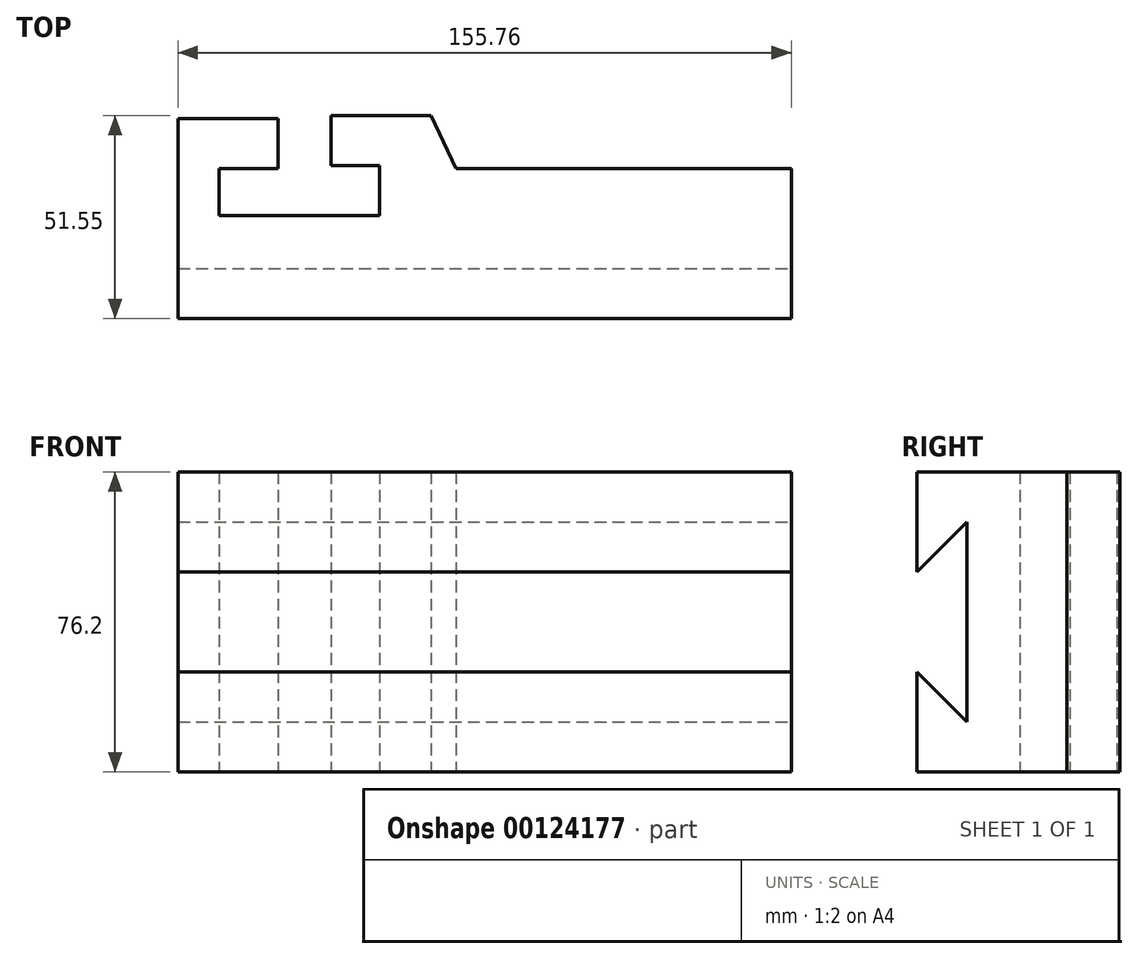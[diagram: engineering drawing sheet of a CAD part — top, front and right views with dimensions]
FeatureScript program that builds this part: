
annotation { "Feature Type Name" : "Feature", "Feature Type Description" : "" }
export const myFeature = defineFeature(function(context is Context, id is Id, definition is map)
    precondition{}
    {
        {
            var Q0;
            Q0=qCreatedBy(makeId("Top.planeOp"),FACE);
            var sketch = newSketch(context, id + "F0", { "sketchPlane" : qUnion([Q0])});
            skLineSegment(sketch, "E0", {"start": v(-101.7, 36.36) * mm, "end": v(-76.3, 36.36) * mm});
            skLineSegment(sketch, "E1", {"start": v(-76.3, 36.36) * mm, "end": v(-76.3, 23.66) * mm});
            skLineSegment(sketch, "E2", {"start": v(-76.3, 23.66) * mm, "end": v(-91.24, 23.66) * mm});
            skLineSegment(sketch, "E3", {"start": v(-91.24, 23.66) * mm, "end": v(-91.24, 11.7) * mm});
            skLineSegment(sketch, "E4", {"start": v(-91.24, 11.7) * mm, "end": v(-50.52, 11.7) * mm});
            skLineSegment(sketch, "E5", {"start": v(-50.52, 11.7) * mm, "end": v(-50.52, 24.4) * mm});
            skLineSegment(sketch, "E6", {"start": v(-50.52, 24.4) * mm, "end": v(-62.85, 24.4) * mm});
            skLineSegment(sketch, "E7", {"start": v(-62.85, 24.4) * mm, "end": v(-62.85, 37.1) * mm});
            skLineSegment(sketch, "E8", {"start": v(-62.85, 37.1) * mm, "end": v(-37.45, 37.1) * mm});
            skLineSegment(sketch, "E9", {"start": v(-37.45, 37.1) * mm, "end": v(-31.1, 23.66) * mm});
            skLineSegment(sketch, "E10", {"start": v(-31.1, 23.66) * mm, "end": v(54.06, 23.66) * mm});
            skLineSegment(sketch, "E11", {"start": v(54.06, 23.66) * mm, "end": v(54.06, -14.44) * mm});
            skLineSegment(sketch, "E12", {"start": v(-101.7, -14.44) * mm, "end": v(-101.7, 36.36) * mm});
            skLineSegment(sketch, "E13", {"start": v(-101.7, -14.44) * mm, "end": v(54.06, -14.44) * mm});
            skSolve(sketch);
        }
        {
            var Q0;
            Q0=makeQuery(id+"F0.imprint","IMPRINT",FACE,{"disambiguationData":[TD([[makeQuery(id+"F0.imprint","IMPRINT",EDGE,{"derivedFrom":sQuery(id+"F0.wireOp",EDGE,"E0")}),-1.0]])]});
            extrude(context, id + "F1", {"entities" : qUnion([Q0]), "depth" : 76.2 * mm});
        }
        {
            var Q0;
            Q0=makeQuery(id+"F1.opExtrude","SWEPT_FACE",FACE,{"disambiguationData":[OSD([sQuery(id+"F0.wireOp",EDGE,"E11")])]});
            var sketch = newSketch(context, id + "F2", { "sketchPlane" : qUnion([Q0])});
            skLineSegment(sketch, "E14", {"start": v(-14.44, 25.4) * mm, "end": v(-1.74, 12.7) * mm});
            skLineSegment(sketch, "E15", {"start": v(-1.74, 12.7) * mm, "end": v(-1.74, 63.5) * mm});
            skLineSegment(sketch, "E16", {"start": v(-1.74, 63.5) * mm, "end": v(-14.44, 50.8) * mm});
            skLineSegment(sketch, "E17", {"start": v(-14.44, 50.8) * mm, "end": v(-14.44, 25.4) * mm});
            skLineSegment(sketch, "E18", {"start": v(-14.44, 76.2) * mm, "end": v(-14.44, 50.8) * mm});
            skLineSegment(sketch, "E19", {"start": v(-14.44, 25.4) * mm, "end": v(-14.44, 0) * mm});
            skSolve(sketch);
        }
        {
            var Q0;
            Q0=makeQuery(id+"F2.imprint","IMPRINT",FACE,{"disambiguationData":[TD([[makeQuery(id+"F2.imprint","IMPRINT",EDGE,{"derivedFrom":sQuery(id+"F2.wireOp",EDGE,"E14")}),1.0]])]});
            extrude(context, id + "F3", {"entities" : qUnion([Q0]), "operationType" : NewBodyOperationType.REMOVE, "endBound" : BoundingType.THROUGH_ALL, "oppositeDirection" : true, "depth" : 25.4 * mm});
        }
    });
